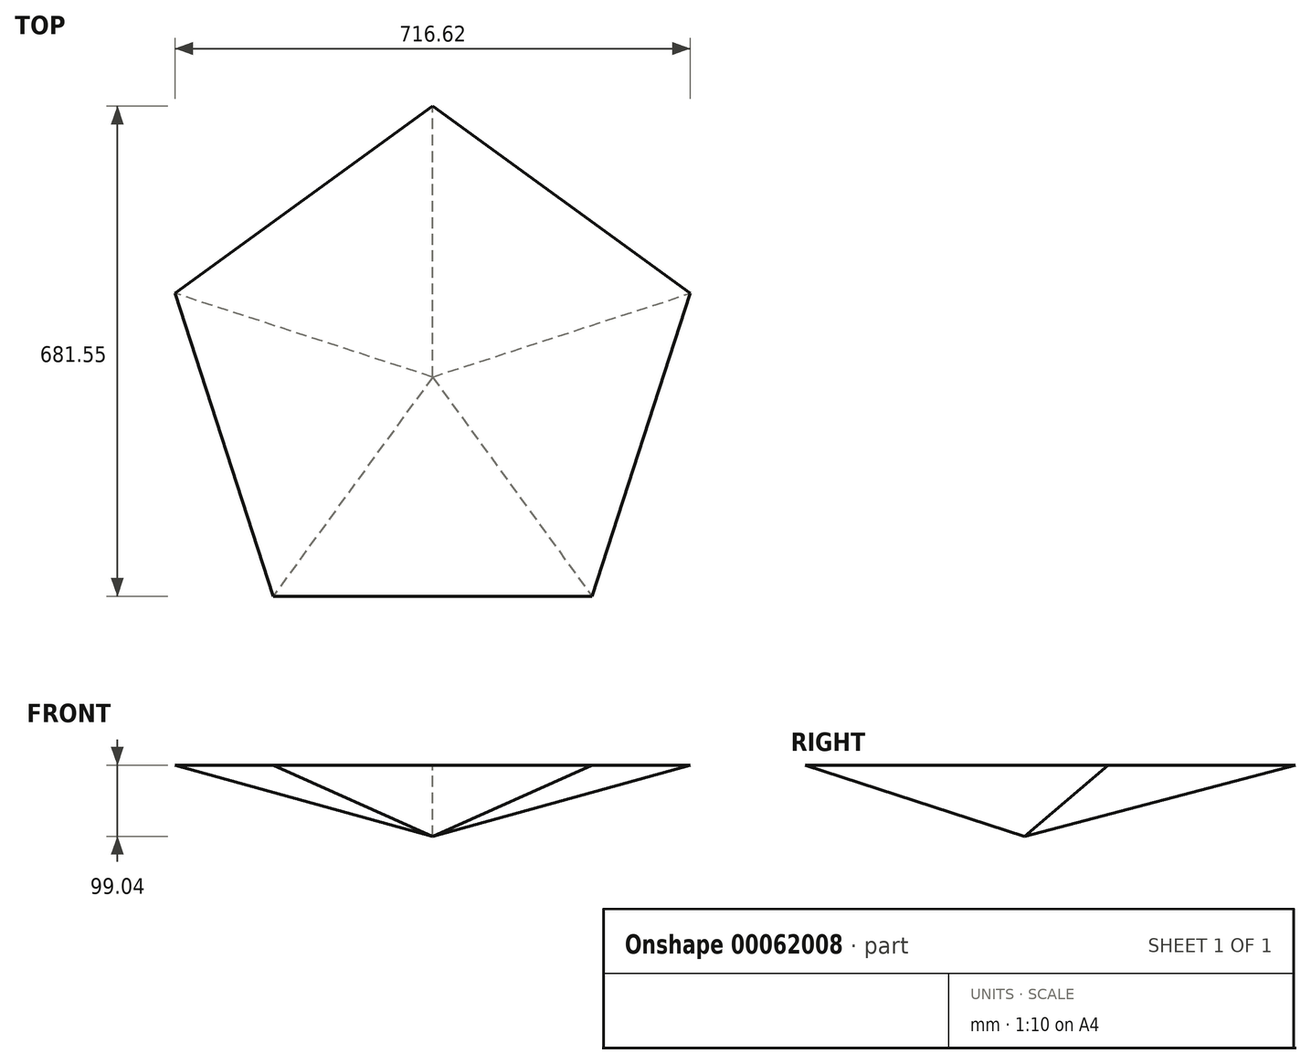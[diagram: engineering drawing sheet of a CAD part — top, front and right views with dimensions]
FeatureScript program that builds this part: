
annotation { "Feature Type Name" : "Feature", "Feature Type Description" : "" }
export const myFeature = defineFeature(function(context is Context, id is Id, definition is map)
    precondition{}
    {
        {
            var Q0;
            Q0=qCreatedBy(makeId("Top.planeOp"),FACE);
            var sketch = newSketch(context, id + "F0", { "sketchPlane" : qUnion([Q0])});
            skCircle(sketch, "E0.cCircle", {"center": v(0, 0) * mm, "radius": 304.8 * mm, "construction": true});
            skLineSegment(sketch, "E0.0", {"start": v(221.45, -304.8) * mm, "end": v(-221.45, -304.8) * mm});
            skLineSegment(sketch, "E0.1", {"start": v(-221.45, -304.8) * mm, "end": v(-358.31, 116.42) * mm});
            skLineSegment(sketch, "E0.2", {"start": v(-358.31, 116.42) * mm, "end": v(0, 376.75) * mm});
            skLineSegment(sketch, "E0.3", {"start": v(0, 376.75) * mm, "end": v(358.31, 116.42) * mm});
            skLineSegment(sketch, "E0.4", {"start": v(358.31, 116.42) * mm, "end": v(221.45, -304.8) * mm});
            skPoint(sketch, "E0.0.midPoint", {"position": v(0, -304.8) * mm});
            skSolve(sketch);
        }
        {
            var Q0;
            Q0 = qSketchRegion(id + "F0", true);
            extrude(context, id + "F1", {"entities" : qUnion([Q0]), "oppositeDirection" : true, "depth" : 101.6 * mm, "hasDraft" : true, "draftAngle" : 72 * degree, "draftPullDirection" : true});
        }
    });
